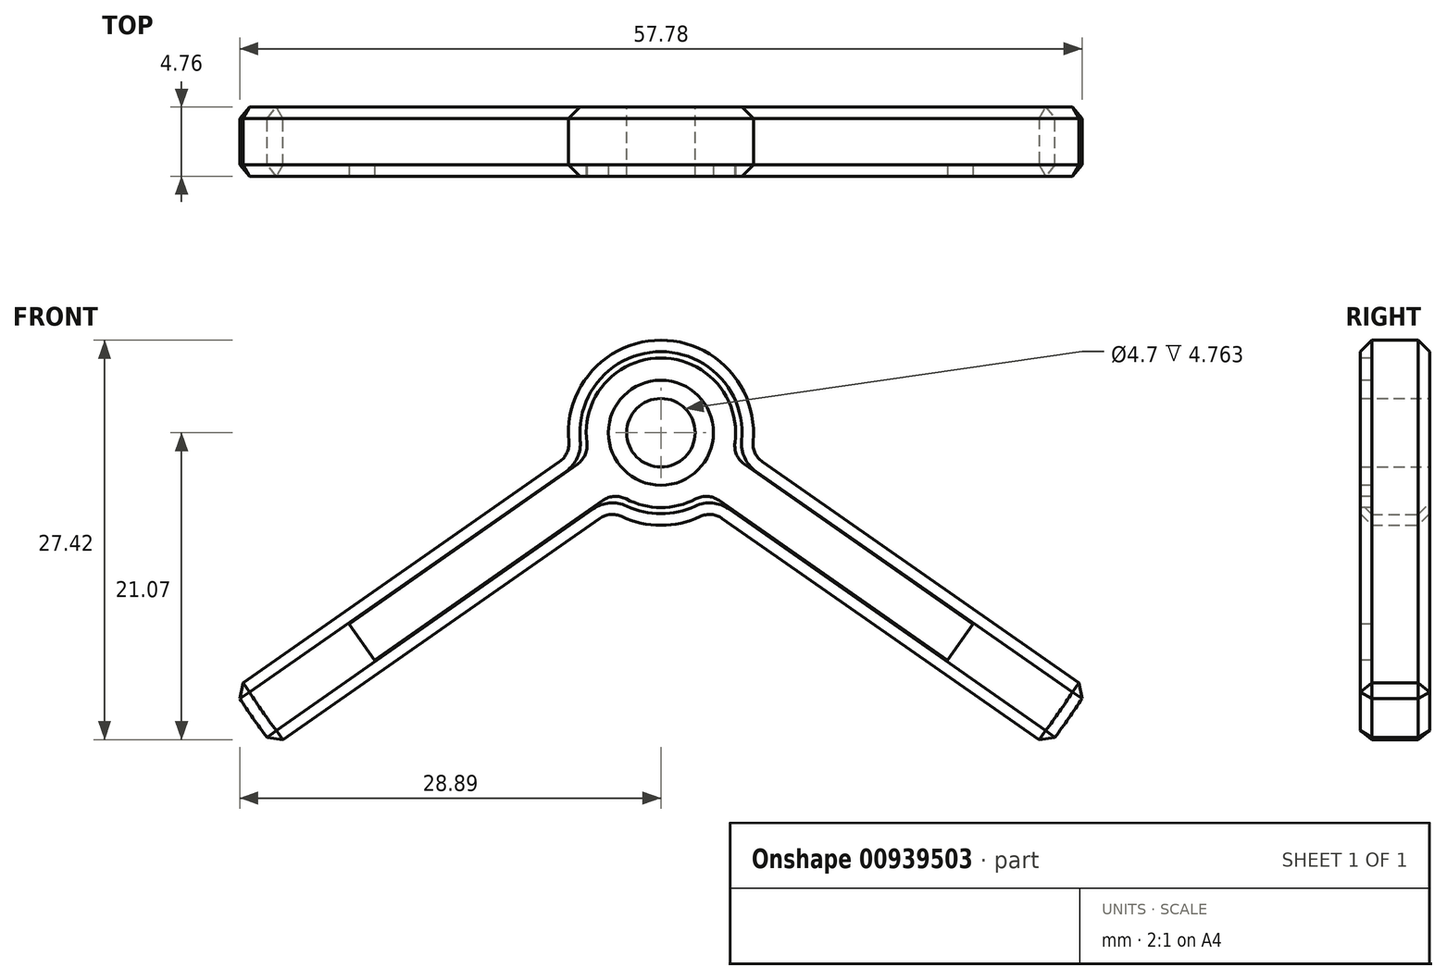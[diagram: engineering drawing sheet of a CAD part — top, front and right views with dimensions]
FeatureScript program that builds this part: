
annotation { "Feature Type Name" : "Feature", "Feature Type Description" : "" }
export const myFeature = defineFeature(function(context is Context, id is Id, definition is map)
    precondition{}
    {
        {
            var Q0;
            Q0=qCreatedBy(makeId("Front.planeOp"),FACE);
            var sketch = newSketch(context, id + "F0", { "sketchPlane" : qUnion([Q0])});
            skArc(sketch, "E0", {"start": v(-3.43, -5.34) * mm, "mid": v(0, -6.35) * mm, "end": v(3.43, -5.34) * mm});
            skLineSegment(sketch, "E1", {"start": v(-29.28, -17.6) * mm, "end": v(-6.18, -1.45) * mm});
            skLineSegment(sketch, "E2.MirrorCS", {"start": v(-26.55, -21.5) * mm, "end": v(-3.43, -5.34) * mm});
            skPoint(sketch, "E3.orphan", {"position": v(-28.95, -23.18) * mm});
            skPoint(sketch, "E4.orphan", {"position": v(-31.68, -19.27) * mm});
            skArc(sketch, "E5.converted", {"start": v(-29.28, -17.6) * mm, "mid": v(-27.98, -19.6) * mm, "end": v(-26.55, -21.5) * mm});
            skLineSegment(sketch, "E6", {"start": v(0, 0) * mm, "end": v(0, -27.71) * mm, "construction": true});
            skLineSegment(sketch, "E7.MirrorCS", {"start": v(26.55, -21.5) * mm, "end": v(3.43, -5.34) * mm});
            skLineSegment(sketch, "E8.MirrorCS", {"start": v(29.28, -17.6) * mm, "end": v(6.18, -1.45) * mm});
            skArc(sketch, "E9.MirrorCS", {"start": v(29.28, -17.6) * mm, "mid": v(27.98, -19.6) * mm, "end": v(26.55, -21.5) * mm});
            skCircle(sketch, "E10", {"center": v(0, 0) * mm, "radius": 2.35 * mm});
            skLineSegment(sketch, "E11", {"start": v(0, 0) * mm, "end": v(-27.98, -19.6) * mm, "construction": true});
            skArc(sketch, "E12.trimOffspring", {"start": v(6.18, -1.45) * mm, "mid": v(0, 6.35) * mm, "end": v(-6.18, -1.45) * mm});
            skSolve(sketch);
        }
        {
            var Q0;
            Q0=makeQuery(id+"F0.imprint","IMPRINT",FACE,{"disambiguationData":[TD([[makeQuery(id+"F0.imprint","IMPRINT",EDGE,{"derivedFrom":sQuery(id+"F0.wireOp",EDGE,"E0")}),1.0]])]});
            extrude(context, id + "F1", {"entities" : qUnion([Q0]), "depth" : 4.76 * mm, "offsetDistance" : 25.4 * mm});
        }
        {
            var Q0;
            Q0=makeQuery(id+"F1.opExtrude","SWEPT_EDGE",EDGE,{"disambiguationData":[OSD([sQuery(id+"F0.wireOp",EDGE,"E8.MirrorCS"),sQuery(id+"F0.wireOp",EDGE,"E12.trimOffspring")])]});
            var Q1;
            Q1=makeQuery(id+"F1.opExtrude","SWEPT_EDGE",EDGE,{"disambiguationData":[OSD([sQuery(id+"F0.wireOp",EDGE,"E1"),sQuery(id+"F0.wireOp",EDGE,"E12.trimOffspring")])]});
            var Q2;
            Q2=makeQuery(id+"F1.opExtrude","SWEPT_EDGE",EDGE,{"disambiguationData":[OSD([sQuery(id+"F0.wireOp",EDGE,"E0"),sQuery(id+"F0.wireOp",EDGE,"E2.MirrorCS")])]});
            var Q3;
            Q3=makeQuery(id+"F1.opExtrude","SWEPT_EDGE",EDGE,{"disambiguationData":[OSD([sQuery(id+"F0.wireOp",EDGE,"E0"),sQuery(id+"F0.wireOp",EDGE,"E7.MirrorCS")])]});
            fillet(context, id + "F2", {"entities" : qUnion([Q0, Q1, Q2, Q3]), "radius" : 1.52 * mm, "tangentPropagation" : true, "allowEdgeOverflow" : false});
        }
        {
            var Q0;
            Q0=makeQuery(id+"F1.opExtrude","CAP_FACE",FACE,{"disambiguationData":[OSD([sQuery(id+"F0.wireOp",EDGE,"E0"),sQuery(id+"F0.wireOp",EDGE,"E1"),sQuery(id+"F0.wireOp",EDGE,"E2.MirrorCS"),sQuery(id+"F0.wireOp",EDGE,"E5.converted"),sQuery(id+"F0.wireOp",EDGE,"E7.MirrorCS"),sQuery(id+"F0.wireOp",EDGE,"E8.MirrorCS"),sQuery(id+"F0.wireOp",EDGE,"E9.MirrorCS"),sQuery(id+"F0.wireOp",EDGE,"E10"),sQuery(id+"F0.wireOp",EDGE,"E12.trimOffspring")])],"isStart":false});
            var sketch = newSketch(context, id + "F3", { "sketchPlane" : qUnion([Q0])});
            skLineSegment(sketch, "E13", {"start": v(-3.58, -2.5) * mm, "end": v(-27.98, -19.6) * mm, "construction": true});
            skCircle(sketch, "E14", {"center": v(0, 0) * mm, "radius": 4.37 * mm, "construction": true});
            skLineSegment(sketch, "E15", {"start": v(3.58, -2.5) * mm, "end": v(27.98, -19.6) * mm, "construction": true});
            skCircle(sketch, "E16", {"center": v(-21.8, -15.27) * mm, "radius": 0.7 * mm, "construction": true});
            skLineSegment(sketch, "E17", {"start": v(0, 0) * mm, "end": v(0, -22.55) * mm, "construction": true});
            skCircle(sketch, "E18.MirrorC", {"center": v(21.8, -15.27) * mm, "radius": 0.7 * mm, "construction": true});
            skLineSegment(sketch, "E19", {"start": v(-21.4, -13.12) * mm, "end": v(-5.72, -2.14) * mm});
            skArc(sketch, "E20", {"start": v(5.08, -0.69) * mm, "mid": v(0, 5.13) * mm, "end": v(-5.08, -0.69) * mm});
            skArc(sketch, "E21.filletArc", {"start": v(-5.72, -2.14) * mm, "mid": v(-5.2, -1.5) * mm, "end": v(-5.08, -0.69) * mm});
            skLineSegment(sketch, "E22.MirrorCS", {"start": v(-19.65, -15.62) * mm, "end": v(-3.97, -4.64) * mm});
            skLineSegment(sketch, "E23", {"start": v(-21.4, -13.12) * mm, "end": v(-19.65, -15.62) * mm});
            skLineSegment(sketch, "E24.MirrorCS", {"start": v(19.65, -15.62) * mm, "end": v(3.97, -4.64) * mm});
            skLineSegment(sketch, "E25.MirrorCS", {"start": v(21.4, -13.12) * mm, "end": v(5.72, -2.14) * mm});
            skLineSegment(sketch, "E26.MirrorCS", {"start": v(21.4, -13.12) * mm, "end": v(19.65, -15.62) * mm});
            skArc(sketch, "E27", {"start": v(-2.39, -4.54) * mm, "mid": v(0, -5.13) * mm, "end": v(2.39, -4.54) * mm});
            skPoint(sketch, "E28.newPointA", {"position": v(-3.97, -4.64) * mm});
            skArc(sketch, "E28.filletArc", {"start": v(-2.39, -4.54) * mm, "mid": v(-3.2, -4.37) * mm, "end": v(-3.97, -4.64) * mm});
            skPoint(sketch, "E29.newPointA", {"position": v(3.97, -4.64) * mm});
            skArc(sketch, "E29.filletArc", {"start": v(3.97, -4.64) * mm, "mid": v(3.2, -4.37) * mm, "end": v(2.39, -4.54) * mm});
            skPoint(sketch, "E30.newPointB", {"position": v(5.72, -2.14) * mm});
            skArc(sketch, "E30.filletArc", {"start": v(5.08, -0.69) * mm, "mid": v(5.2, -1.5) * mm, "end": v(5.72, -2.14) * mm});
            skCircle(sketch, "E31", {"center": v(0, 0) * mm, "radius": 3.6 * mm});
            skSolve(sketch);
        }
        {
            var Q0;
            Q0 = qSketchRegion(id + "F3", true);
            extrude(context, id + "F4", {"entities" : qUnion([Q0]), "operationType" : NewBodyOperationType.REMOVE, "oppositeDirection" : true, "depth" : 0.79 * mm, "offsetDistance" : 25.4 * mm});
        }
        {
            var Q0;
            Q0=makeQuery(id+"F1.opExtrude","CAP_EDGE",EDGE,{"disambiguationData":[OSD([sQuery(id+"F0.wireOp",EDGE,"E1")])],"isStart":false});
            var Q1;
            Q1=makeQuery(id+"F1.opExtrude","CAP_EDGE",EDGE,{"disambiguationData":[OSD([sQuery(id+"F0.wireOp",EDGE,"E5.converted")])],"isStart":false});
            var Q2;
            Q2=makeQuery(id+"F1.opExtrude","CAP_EDGE",EDGE,{"disambiguationData":[OSD([sQuery(id+"F0.wireOp",EDGE,"E2.MirrorCS")])],"isStart":false});
            var Q3;
            Q3=makeQuery(id+"F1.opExtrude","CAP_EDGE",EDGE,{"disambiguationData":[OSD([sQuery(id+"F0.wireOp",EDGE,"E0")])],"isStart":false});
            var Q4;
            {var subQ0=sQuery(id+"F0.wireOp",EDGE,"E2.MirrorCS");var subQ1=sQuery(id+"F0.wireOp",EDGE,"E0");Q4=makeQuery(id+"F2.opFillet","BLEND_EDGE",EDGE,{"blendedFrom":[makeQuery(id+"F1.opExtrude","SWEPT_EDGE",EDGE,{"disambiguationData":[OSD([subQ1,subQ0])]}),makeQuery(id+"F1.opExtrude","CAP_FACE",FACE,{"disambiguationData":[OSD([subQ1,sQuery(id+"F0.wireOp",EDGE,"E1"),subQ0,sQuery(id+"F0.wireOp",EDGE,"E5.converted"),sQuery(id+"F0.wireOp",EDGE,"E7.MirrorCS"),sQuery(id+"F0.wireOp",EDGE,"E8.MirrorCS"),sQuery(id+"F0.wireOp",EDGE,"E9.MirrorCS"),sQuery(id+"F0.wireOp",EDGE,"E10"),sQuery(id+"F0.wireOp",EDGE,"E12.trimOffspring")])],"isStart":false})],"blendedInto":[makeQuery(id+"F1.opExtrude","CAP_FACE",FACE,{"disambiguationData":[OSD([subQ1,sQuery(id+"F0.wireOp",EDGE,"E1"),subQ0,sQuery(id+"F0.wireOp",EDGE,"E5.converted"),sQuery(id+"F0.wireOp",EDGE,"E7.MirrorCS"),sQuery(id+"F0.wireOp",EDGE,"E8.MirrorCS"),sQuery(id+"F0.wireOp",EDGE,"E9.MirrorCS"),sQuery(id+"F0.wireOp",EDGE,"E10"),sQuery(id+"F0.wireOp",EDGE,"E12.trimOffspring")])],"isStart":false})]});}
            var Q5;
            Q5=makeQuery(id+"F1.opExtrude","CAP_EDGE",EDGE,{"disambiguationData":[OSD([sQuery(id+"F0.wireOp",EDGE,"E12.trimOffspring")])],"isStart":false});
            var Q6;
            {var subQ0=sQuery(id+"F0.wireOp",EDGE,"E12.trimOffspring");var subQ1=sQuery(id+"F0.wireOp",EDGE,"E8.MirrorCS");Q6=makeQuery(id+"F2.opFillet","BLEND_EDGE",EDGE,{"blendedFrom":[makeQuery(id+"F1.opExtrude","SWEPT_EDGE",EDGE,{"disambiguationData":[OSD([subQ1,subQ0])]}),makeQuery(id+"F1.opExtrude","CAP_FACE",FACE,{"disambiguationData":[OSD([sQuery(id+"F0.wireOp",EDGE,"E0"),sQuery(id+"F0.wireOp",EDGE,"E1"),sQuery(id+"F0.wireOp",EDGE,"E2.MirrorCS"),sQuery(id+"F0.wireOp",EDGE,"E5.converted"),sQuery(id+"F0.wireOp",EDGE,"E7.MirrorCS"),subQ1,sQuery(id+"F0.wireOp",EDGE,"E9.MirrorCS"),sQuery(id+"F0.wireOp",EDGE,"E10"),subQ0])],"isStart":false})],"blendedInto":[makeQuery(id+"F1.opExtrude","CAP_FACE",FACE,{"disambiguationData":[OSD([sQuery(id+"F0.wireOp",EDGE,"E0"),sQuery(id+"F0.wireOp",EDGE,"E1"),sQuery(id+"F0.wireOp",EDGE,"E2.MirrorCS"),sQuery(id+"F0.wireOp",EDGE,"E5.converted"),sQuery(id+"F0.wireOp",EDGE,"E7.MirrorCS"),subQ1,sQuery(id+"F0.wireOp",EDGE,"E9.MirrorCS"),sQuery(id+"F0.wireOp",EDGE,"E10"),subQ0])],"isStart":false})]});}
            var Q7;
            Q7=makeQuery(id+"F1.opExtrude","CAP_EDGE",EDGE,{"disambiguationData":[OSD([sQuery(id+"F0.wireOp",EDGE,"E8.MirrorCS")])],"isStart":true});
            var Q8;
            Q8=makeQuery(id+"F1.opExtrude","CAP_EDGE",EDGE,{"disambiguationData":[OSD([sQuery(id+"F0.wireOp",EDGE,"E8.MirrorCS")])],"isStart":false});
            var Q9;
            Q9=makeQuery(id+"F1.opExtrude","SWEPT_EDGE",EDGE,{"disambiguationData":[OSD([sQuery(id+"F0.wireOp",EDGE,"E8.MirrorCS"),sQuery(id+"F0.wireOp",EDGE,"E9.MirrorCS")])]});
            var Q10;
            Q10=makeQuery(id+"F1.opExtrude","CAP_EDGE",EDGE,{"disambiguationData":[OSD([sQuery(id+"F0.wireOp",EDGE,"E12.trimOffspring")])],"isStart":true});
            var Q11;
            {var subQ0=sQuery(id+"F0.wireOp",EDGE,"E12.trimOffspring");var subQ1=sQuery(id+"F0.wireOp",EDGE,"E8.MirrorCS");Q11=makeQuery(id+"F2.opFillet","BLEND_EDGE",EDGE,{"blendedFrom":[makeQuery(id+"F1.opExtrude","SWEPT_EDGE",EDGE,{"disambiguationData":[OSD([subQ1,subQ0])]}),makeQuery(id+"F1.opExtrude","CAP_FACE",FACE,{"disambiguationData":[OSD([sQuery(id+"F0.wireOp",EDGE,"E0"),sQuery(id+"F0.wireOp",EDGE,"E1"),sQuery(id+"F0.wireOp",EDGE,"E2.MirrorCS"),sQuery(id+"F0.wireOp",EDGE,"E5.converted"),sQuery(id+"F0.wireOp",EDGE,"E7.MirrorCS"),subQ1,sQuery(id+"F0.wireOp",EDGE,"E9.MirrorCS"),sQuery(id+"F0.wireOp",EDGE,"E10"),subQ0])],"isStart":true})],"blendedInto":[makeQuery(id+"F1.opExtrude","CAP_FACE",FACE,{"disambiguationData":[OSD([sQuery(id+"F0.wireOp",EDGE,"E0"),sQuery(id+"F0.wireOp",EDGE,"E1"),sQuery(id+"F0.wireOp",EDGE,"E2.MirrorCS"),sQuery(id+"F0.wireOp",EDGE,"E5.converted"),sQuery(id+"F0.wireOp",EDGE,"E7.MirrorCS"),subQ1,sQuery(id+"F0.wireOp",EDGE,"E9.MirrorCS"),sQuery(id+"F0.wireOp",EDGE,"E10"),subQ0])],"isStart":true})]});}
            var Q12;
            {var subQ0=sQuery(id+"F0.wireOp",EDGE,"E12.trimOffspring");var subQ1=sQuery(id+"F0.wireOp",EDGE,"E1");Q12=makeQuery(id+"F2.opFillet","BLEND_EDGE",EDGE,{"blendedFrom":[makeQuery(id+"F1.opExtrude","SWEPT_EDGE",EDGE,{"disambiguationData":[OSD([subQ1,subQ0])]}),makeQuery(id+"F1.opExtrude","CAP_FACE",FACE,{"disambiguationData":[OSD([sQuery(id+"F0.wireOp",EDGE,"E0"),subQ1,sQuery(id+"F0.wireOp",EDGE,"E2.MirrorCS"),sQuery(id+"F0.wireOp",EDGE,"E5.converted"),sQuery(id+"F0.wireOp",EDGE,"E7.MirrorCS"),sQuery(id+"F0.wireOp",EDGE,"E8.MirrorCS"),sQuery(id+"F0.wireOp",EDGE,"E9.MirrorCS"),sQuery(id+"F0.wireOp",EDGE,"E10"),subQ0])],"isStart":false})],"blendedInto":[makeQuery(id+"F1.opExtrude","CAP_FACE",FACE,{"disambiguationData":[OSD([sQuery(id+"F0.wireOp",EDGE,"E0"),subQ1,sQuery(id+"F0.wireOp",EDGE,"E2.MirrorCS"),sQuery(id+"F0.wireOp",EDGE,"E5.converted"),sQuery(id+"F0.wireOp",EDGE,"E7.MirrorCS"),sQuery(id+"F0.wireOp",EDGE,"E8.MirrorCS"),sQuery(id+"F0.wireOp",EDGE,"E9.MirrorCS"),sQuery(id+"F0.wireOp",EDGE,"E10"),subQ0])],"isStart":false})]});}
            var Q13;
            Q13=makeQuery(id+"F1.opExtrude","CAP_EDGE",EDGE,{"disambiguationData":[OSD([sQuery(id+"F0.wireOp",EDGE,"E1")])],"isStart":true});
            var Q14;
            Q14=makeQuery(id+"F1.opExtrude","CAP_EDGE",EDGE,{"disambiguationData":[OSD([sQuery(id+"F0.wireOp",EDGE,"E9.MirrorCS")])],"isStart":false});
            var Q15;
            Q15=makeQuery(id+"F1.opExtrude","SWEPT_EDGE",EDGE,{"disambiguationData":[OSD([sQuery(id+"F0.wireOp",EDGE,"E7.MirrorCS"),sQuery(id+"F0.wireOp",EDGE,"E9.MirrorCS")])]});
            var Q16;
            Q16=makeQuery(id+"F1.opExtrude","CAP_EDGE",EDGE,{"disambiguationData":[OSD([sQuery(id+"F0.wireOp",EDGE,"E9.MirrorCS")])],"isStart":true});
            var Q17;
            Q17=makeQuery(id+"F1.opExtrude","CAP_EDGE",EDGE,{"disambiguationData":[OSD([sQuery(id+"F0.wireOp",EDGE,"E7.MirrorCS")])],"isStart":false});
            var Q18;
            {var subQ0=sQuery(id+"F0.wireOp",EDGE,"E7.MirrorCS");var subQ1=sQuery(id+"F0.wireOp",EDGE,"E0");Q18=makeQuery(id+"F2.opFillet","BLEND_EDGE",EDGE,{"blendedFrom":[makeQuery(id+"F1.opExtrude","SWEPT_EDGE",EDGE,{"disambiguationData":[OSD([subQ1,subQ0])]}),makeQuery(id+"F1.opExtrude","CAP_FACE",FACE,{"disambiguationData":[OSD([subQ1,sQuery(id+"F0.wireOp",EDGE,"E1"),sQuery(id+"F0.wireOp",EDGE,"E2.MirrorCS"),sQuery(id+"F0.wireOp",EDGE,"E5.converted"),subQ0,sQuery(id+"F0.wireOp",EDGE,"E8.MirrorCS"),sQuery(id+"F0.wireOp",EDGE,"E9.MirrorCS"),sQuery(id+"F0.wireOp",EDGE,"E10"),sQuery(id+"F0.wireOp",EDGE,"E12.trimOffspring")])],"isStart":false})],"blendedInto":[makeQuery(id+"F1.opExtrude","CAP_FACE",FACE,{"disambiguationData":[OSD([subQ1,sQuery(id+"F0.wireOp",EDGE,"E1"),sQuery(id+"F0.wireOp",EDGE,"E2.MirrorCS"),sQuery(id+"F0.wireOp",EDGE,"E5.converted"),subQ0,sQuery(id+"F0.wireOp",EDGE,"E8.MirrorCS"),sQuery(id+"F0.wireOp",EDGE,"E9.MirrorCS"),sQuery(id+"F0.wireOp",EDGE,"E10"),sQuery(id+"F0.wireOp",EDGE,"E12.trimOffspring")])],"isStart":false})]});}
            var Q19;
            {var subQ0=sQuery(id+"F0.wireOp",EDGE,"E12.trimOffspring");var subQ1=sQuery(id+"F0.wireOp",EDGE,"E1");Q19=makeQuery(id+"F2.opFillet","BLEND_EDGE",EDGE,{"blendedFrom":[makeQuery(id+"F1.opExtrude","SWEPT_EDGE",EDGE,{"disambiguationData":[OSD([subQ1,subQ0])]}),makeQuery(id+"F1.opExtrude","CAP_FACE",FACE,{"disambiguationData":[OSD([sQuery(id+"F0.wireOp",EDGE,"E0"),subQ1,sQuery(id+"F0.wireOp",EDGE,"E2.MirrorCS"),sQuery(id+"F0.wireOp",EDGE,"E5.converted"),sQuery(id+"F0.wireOp",EDGE,"E7.MirrorCS"),sQuery(id+"F0.wireOp",EDGE,"E8.MirrorCS"),sQuery(id+"F0.wireOp",EDGE,"E9.MirrorCS"),sQuery(id+"F0.wireOp",EDGE,"E10"),subQ0])],"isStart":true})],"blendedInto":[makeQuery(id+"F1.opExtrude","CAP_FACE",FACE,{"disambiguationData":[OSD([sQuery(id+"F0.wireOp",EDGE,"E0"),subQ1,sQuery(id+"F0.wireOp",EDGE,"E2.MirrorCS"),sQuery(id+"F0.wireOp",EDGE,"E5.converted"),sQuery(id+"F0.wireOp",EDGE,"E7.MirrorCS"),sQuery(id+"F0.wireOp",EDGE,"E8.MirrorCS"),sQuery(id+"F0.wireOp",EDGE,"E9.MirrorCS"),sQuery(id+"F0.wireOp",EDGE,"E10"),subQ0])],"isStart":true})]});}
            var Q20;
            Q20=makeQuery(id+"F1.opExtrude","CAP_EDGE",EDGE,{"disambiguationData":[OSD([sQuery(id+"F0.wireOp",EDGE,"E7.MirrorCS")])],"isStart":true});
            var Q21;
            Q21=makeQuery(id+"F1.opExtrude","CAP_EDGE",EDGE,{"disambiguationData":[OSD([sQuery(id+"F0.wireOp",EDGE,"E0")])],"isStart":true});
            var Q22;
            {var subQ0=sQuery(id+"F0.wireOp",EDGE,"E7.MirrorCS");var subQ1=sQuery(id+"F0.wireOp",EDGE,"E0");Q22=makeQuery(id+"F2.opFillet","BLEND_EDGE",EDGE,{"blendedFrom":[makeQuery(id+"F1.opExtrude","SWEPT_EDGE",EDGE,{"disambiguationData":[OSD([subQ1,subQ0])]}),makeQuery(id+"F1.opExtrude","CAP_FACE",FACE,{"disambiguationData":[OSD([subQ1,sQuery(id+"F0.wireOp",EDGE,"E1"),sQuery(id+"F0.wireOp",EDGE,"E2.MirrorCS"),sQuery(id+"F0.wireOp",EDGE,"E5.converted"),subQ0,sQuery(id+"F0.wireOp",EDGE,"E8.MirrorCS"),sQuery(id+"F0.wireOp",EDGE,"E9.MirrorCS"),sQuery(id+"F0.wireOp",EDGE,"E10"),sQuery(id+"F0.wireOp",EDGE,"E12.trimOffspring")])],"isStart":true})],"blendedInto":[makeQuery(id+"F1.opExtrude","CAP_FACE",FACE,{"disambiguationData":[OSD([subQ1,sQuery(id+"F0.wireOp",EDGE,"E1"),sQuery(id+"F0.wireOp",EDGE,"E2.MirrorCS"),sQuery(id+"F0.wireOp",EDGE,"E5.converted"),subQ0,sQuery(id+"F0.wireOp",EDGE,"E8.MirrorCS"),sQuery(id+"F0.wireOp",EDGE,"E9.MirrorCS"),sQuery(id+"F0.wireOp",EDGE,"E10"),sQuery(id+"F0.wireOp",EDGE,"E12.trimOffspring")])],"isStart":true})]});}
            var Q23;
            {var subQ0=sQuery(id+"F0.wireOp",EDGE,"E2.MirrorCS");var subQ1=sQuery(id+"F0.wireOp",EDGE,"E0");Q23=makeQuery(id+"F2.opFillet","BLEND_EDGE",EDGE,{"blendedFrom":[makeQuery(id+"F1.opExtrude","SWEPT_EDGE",EDGE,{"disambiguationData":[OSD([subQ1,subQ0])]}),makeQuery(id+"F1.opExtrude","CAP_FACE",FACE,{"disambiguationData":[OSD([subQ1,sQuery(id+"F0.wireOp",EDGE,"E1"),subQ0,sQuery(id+"F0.wireOp",EDGE,"E5.converted"),sQuery(id+"F0.wireOp",EDGE,"E7.MirrorCS"),sQuery(id+"F0.wireOp",EDGE,"E8.MirrorCS"),sQuery(id+"F0.wireOp",EDGE,"E9.MirrorCS"),sQuery(id+"F0.wireOp",EDGE,"E10"),sQuery(id+"F0.wireOp",EDGE,"E12.trimOffspring")])],"isStart":true})],"blendedInto":[makeQuery(id+"F1.opExtrude","CAP_FACE",FACE,{"disambiguationData":[OSD([subQ1,sQuery(id+"F0.wireOp",EDGE,"E1"),subQ0,sQuery(id+"F0.wireOp",EDGE,"E5.converted"),sQuery(id+"F0.wireOp",EDGE,"E7.MirrorCS"),sQuery(id+"F0.wireOp",EDGE,"E8.MirrorCS"),sQuery(id+"F0.wireOp",EDGE,"E9.MirrorCS"),sQuery(id+"F0.wireOp",EDGE,"E10"),sQuery(id+"F0.wireOp",EDGE,"E12.trimOffspring")])],"isStart":true})]});}
            var Q24;
            Q24=makeQuery(id+"F1.opExtrude","CAP_EDGE",EDGE,{"disambiguationData":[OSD([sQuery(id+"F0.wireOp",EDGE,"E2.MirrorCS")])],"isStart":true});
            var Q25;
            Q25=makeQuery(id+"F1.opExtrude","CAP_EDGE",EDGE,{"disambiguationData":[OSD([sQuery(id+"F0.wireOp",EDGE,"E5.converted")])],"isStart":true});
            var Q26;
            Q26=makeQuery(id+"F1.opExtrude","SWEPT_EDGE",EDGE,{"disambiguationData":[OSD([sQuery(id+"F0.wireOp",EDGE,"E2.MirrorCS"),sQuery(id+"F0.wireOp",EDGE,"E5.converted")])]});
            var Q27;
            Q27=makeQuery(id+"F1.opExtrude","SWEPT_EDGE",EDGE,{"disambiguationData":[OSD([sQuery(id+"F0.wireOp",EDGE,"E1"),sQuery(id+"F0.wireOp",EDGE,"E5.converted")])]});
            chamfer(context, id + "F5", {"entities" : qUnion([Q0, Q1, Q2, Q3, Q4, Q5, Q6, Q7, Q8, Q9, Q10, Q11, Q12, Q13, Q14, Q15, Q16, Q17, Q18, Q19, Q20, Q21, Q22, Q23, Q24, Q25, Q26, Q27]), "width" : 0.79 * mm, "tangentPropagation" : true});
        }
    });
